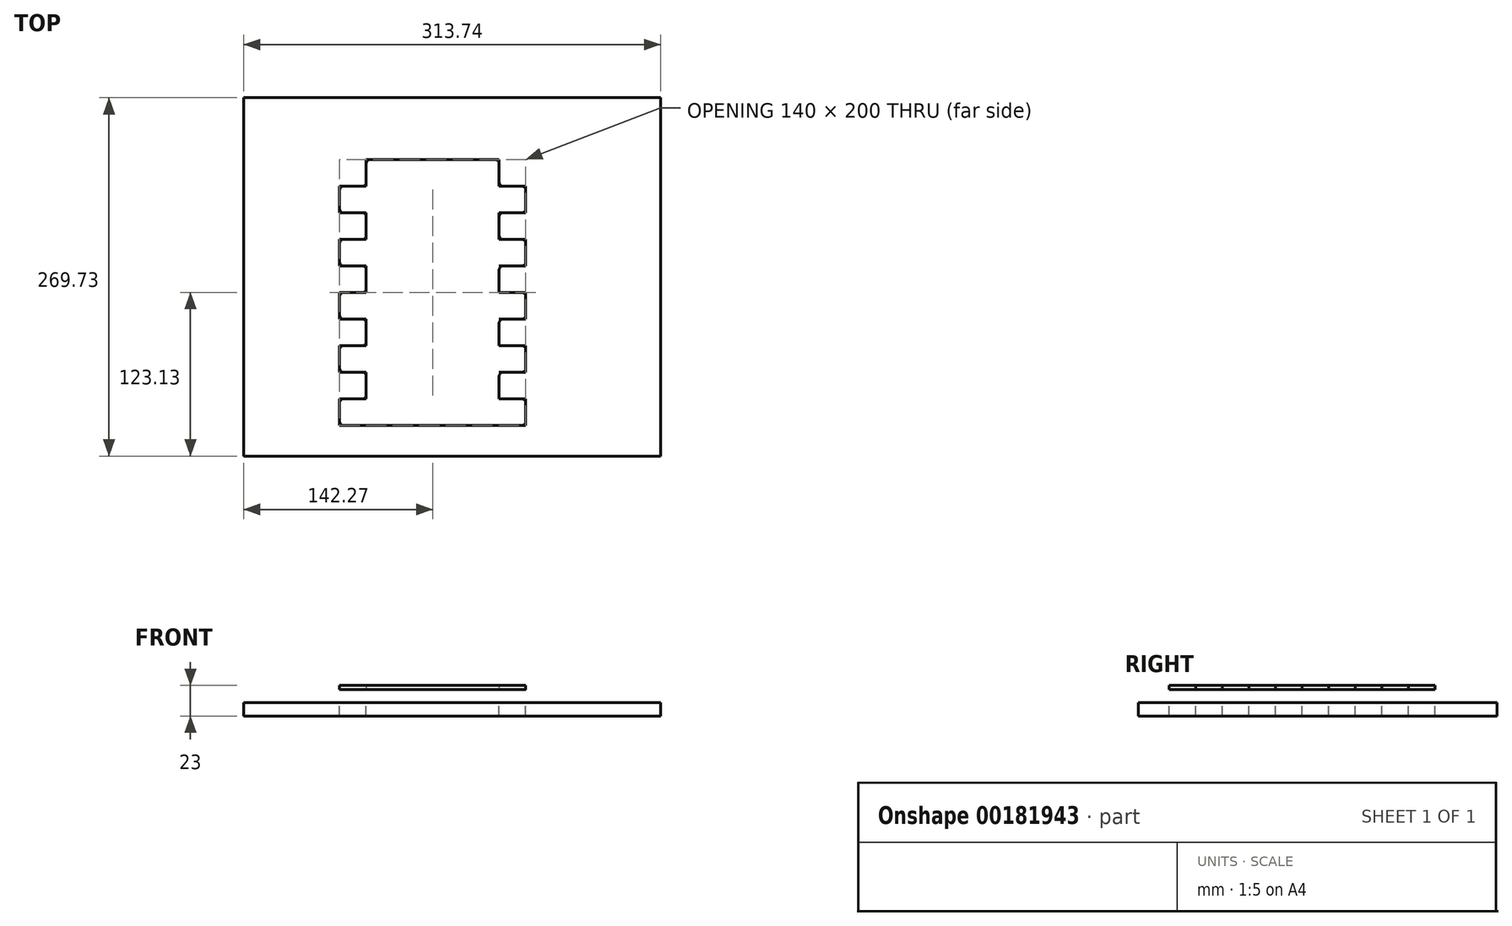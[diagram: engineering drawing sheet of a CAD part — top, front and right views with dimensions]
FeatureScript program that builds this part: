
annotation { "Feature Type Name" : "Feature", "Feature Type Description" : "" }
export const myFeature = defineFeature(function(context is Context, id is Id, definition is map)
    precondition{}
    {
        {
            var Q0;
            Q0=qCreatedBy(makeId("Top.planeOp"),FACE);
            var sketch = newSketch(context, id + "F0", { "sketchPlane" : qUnion([Q0])});
            skLineSegment(sketch, "E0.bottom", {"start": v(0, 0) * mm, "end": v(100, 0) * mm});
            skLineSegment(sketch, "E0.top", {"start": v(0, 200) * mm, "end": v(100, 200) * mm});
            skLineSegment(sketch, "E0.left", {"start": v(0, 0) * mm, "end": v(0, 200) * mm, "construction": true});
            skLineSegment(sketch, "E0.right", {"start": v(100, 0) * mm, "end": v(100, 200) * mm, "construction": true});
            skLineSegment(sketch, "E1.bottom", {"start": v(100, 0) * mm, "end": v(120, 0) * mm});
            skLineSegment(sketch, "E1.top", {"start": v(100, 20) * mm, "end": v(120, 20) * mm});
            skLineSegment(sketch, "E1.left", {"start": v(100, 0) * mm, "end": v(100, 20) * mm, "construction": true});
            skLineSegment(sketch, "E1.right", {"start": v(120, 0) * mm, "end": v(120, 20) * mm});
            skLineSegment(sketch, "E2", {"start": v(50, 0) * mm, "end": v(50, 200) * mm, "construction": true});
            skLineSegment(sketch, "E3.MirrorCS", {"start": v(0, 20) * mm, "end": v(-20, 20) * mm});
            skLineSegment(sketch, "E4.MirrorCS", {"start": v(-20, 0) * mm, "end": v(-20, 20) * mm});
            skLineSegment(sketch, "E5.MirrorCS", {"start": v(0, 0) * mm, "end": v(-20, 0) * mm});
            skLineSegment(sketch, "E6.0.1.0", {"start": v(100, 60) * mm, "end": v(120, 60) * mm});
            skLineSegment(sketch, "E6.0.1.1", {"start": v(120, 40) * mm, "end": v(120, 60) * mm});
            skLineSegment(sketch, "E6.0.1.2", {"start": v(100, 40) * mm, "end": v(120, 40) * mm});
            skLineSegment(sketch, "E6.0.1.3", {"start": v(0, 60) * mm, "end": v(-20, 60) * mm});
            skLineSegment(sketch, "E6.0.1.4", {"start": v(-20, 40) * mm, "end": v(-20, 60) * mm});
            skLineSegment(sketch, "E6.0.1.5", {"start": v(0, 40) * mm, "end": v(-20, 40) * mm});
            skLineSegment(sketch, "E6.0.2.0", {"start": v(100, 100) * mm, "end": v(120, 100) * mm});
            skLineSegment(sketch, "E6.0.2.1", {"start": v(120, 80) * mm, "end": v(120, 100) * mm});
            skLineSegment(sketch, "E6.0.2.2", {"start": v(100, 80) * mm, "end": v(120, 80) * mm});
            skLineSegment(sketch, "E6.0.2.3", {"start": v(0, 100) * mm, "end": v(-20, 100) * mm});
            skLineSegment(sketch, "E6.0.2.4", {"start": v(-20, 80) * mm, "end": v(-20, 100) * mm});
            skLineSegment(sketch, "E6.0.2.5", {"start": v(0, 80) * mm, "end": v(-20, 80) * mm});
            skLineSegment(sketch, "E6.0.3.0", {"start": v(100, 140) * mm, "end": v(120, 140) * mm});
            skLineSegment(sketch, "E6.0.3.1", {"start": v(120, 120) * mm, "end": v(120, 140) * mm});
            skLineSegment(sketch, "E6.0.3.2", {"start": v(100, 120) * mm, "end": v(120, 120) * mm});
            skLineSegment(sketch, "E6.0.3.3", {"start": v(0, 140) * mm, "end": v(-20, 140) * mm});
            skLineSegment(sketch, "E6.0.3.4", {"start": v(-20, 120) * mm, "end": v(-20, 140) * mm});
            skLineSegment(sketch, "E6.0.3.5", {"start": v(0, 120) * mm, "end": v(-20, 120) * mm});
            skLineSegment(sketch, "E6.0.4.0", {"start": v(100, 180) * mm, "end": v(120, 180) * mm});
            skLineSegment(sketch, "E6.0.4.1", {"start": v(120, 160) * mm, "end": v(120, 180) * mm});
            skLineSegment(sketch, "E6.0.4.2", {"start": v(100, 160) * mm, "end": v(120, 160) * mm});
            skLineSegment(sketch, "E6.0.4.3", {"start": v(0, 180) * mm, "end": v(-20, 180) * mm});
            skLineSegment(sketch, "E6.0.4.4", {"start": v(-20, 160) * mm, "end": v(-20, 180) * mm});
            skLineSegment(sketch, "E6.0.4.5", {"start": v(0, 160) * mm, "end": v(-20, 160) * mm});
            skLineSegment(sketch, "E6.direction1", {"start": v(100, 20) * mm, "end": v(125, 20) * mm, "construction": true});
            skLineSegment(sketch, "E6.direction2", {"start": v(100, 20) * mm, "end": v(100, 60) * mm, "construction": true});
            skLineSegment(sketch, "E7", {"start": v(0, 200) * mm, "end": v(0, 180) * mm});
            skLineSegment(sketch, "E8", {"start": v(100, 180) * mm, "end": v(100, 200) * mm});
            skLineSegment(sketch, "E9", {"start": v(100, 20) * mm, "end": v(100, 40) * mm});
            skLineSegment(sketch, "E10", {"start": v(100, 60) * mm, "end": v(100, 80) * mm});
            skLineSegment(sketch, "E11", {"start": v(100, 100) * mm, "end": v(100, 120) * mm});
            skLineSegment(sketch, "E12", {"start": v(100, 140) * mm, "end": v(100, 160) * mm});
            skLineSegment(sketch, "E13", {"start": v(0, 140) * mm, "end": v(0, 160) * mm});
            skLineSegment(sketch, "E14", {"start": v(0, 120) * mm, "end": v(0, 100) * mm});
            skLineSegment(sketch, "E15", {"start": v(0, 80) * mm, "end": v(0, 100) * mm});
            skLineSegment(sketch, "E16", {"start": v(0, 40) * mm, "end": v(0, 20) * mm});
            skLineSegment(sketch, "E17", {"start": v(0, 60) * mm, "end": v(0, 80) * mm});
            skLineSegment(sketch, "E18.bottom", {"start": v(-92.27, -23.13) * mm, "end": v(221.47, -23.13) * mm});
            skLineSegment(sketch, "E18.top", {"start": v(-92.27, 246.6) * mm, "end": v(221.47, 246.6) * mm});
            skLineSegment(sketch, "E18.left", {"start": v(-92.27, -23.13) * mm, "end": v(-92.27, 246.6) * mm});
            skLineSegment(sketch, "E18.right", {"start": v(221.47, -23.13) * mm, "end": v(221.47, 246.6) * mm});
            skSolve(sketch);
        }
        {
            var Q0;
            Q0=makeQuery(id+"F0.imprint","IMPRINT",FACE,{"disambiguationData":[TD([[makeQuery(id+"F0.imprint","IMPRINT",EDGE,{"derivedFrom":sQuery(id+"F0.wireOp",EDGE,"E0.bottom")}),1.0]])]});
            var Q1;
            Q1=makeQuery(id+"F0.imprint","IMPRINT",FACE,{"disambiguationData":[TD([[makeQuery(id+"F0.imprint","IMPRINT",EDGE,{"derivedFrom":sQuery(id+"F0.wireOp",EDGE,"E6.0.2.3")}),1.0]])]});
            extrude(context, id + "F1", {"entities" : qUnion([Q0, Q1]), "depth" : 3 * mm});
        }
        {
            var Q0;
            Q0=makeQuery(id+"F1.opExtrude","SWEPT_EDGE",EDGE,{"disambiguationData":[OSD([sQuery(id+"F0.wireOp",EDGE,"E6.0.4.1"),sQuery(id+"F0.wireOp",EDGE,"E6.0.4.2")])]});
            var Q1;
            Q1=makeQuery(id+"F1.opExtrude","SWEPT_EDGE",EDGE,{"disambiguationData":[OSD([sQuery(id+"F0.wireOp",EDGE,"E6.0.4.2"),sQuery(id+"F0.wireOp",EDGE,"E12")])]});
            var Q2;
            Q2=makeQuery(id+"F1.opExtrude","SWEPT_EDGE",EDGE,{"disambiguationData":[OSD([sQuery(id+"F0.wireOp",EDGE,"E6.0.3.2"),sQuery(id+"F0.wireOp",EDGE,"E11")])]});
            var Q3;
            Q3=makeQuery(id+"F1.opExtrude","SWEPT_EDGE",EDGE,{"disambiguationData":[OSD([sQuery(id+"F0.wireOp",EDGE,"E6.0.2.2"),sQuery(id+"F0.wireOp",EDGE,"E10")])]});
            var Q4;
            Q4=makeQuery(id+"F1.opExtrude","SWEPT_EDGE",EDGE,{"disambiguationData":[OSD([sQuery(id+"F0.wireOp",EDGE,"E6.0.2.1"),sQuery(id+"F0.wireOp",EDGE,"E6.0.2.2")])]});
            var Q5;
            Q5=makeQuery(id+"F1.opExtrude","SWEPT_EDGE",EDGE,{"disambiguationData":[OSD([sQuery(id+"F0.wireOp",EDGE,"E6.0.1.1"),sQuery(id+"F0.wireOp",EDGE,"E6.0.1.2")])]});
            var Q6;
            Q6=makeQuery(id+"F1.opExtrude","SWEPT_EDGE",EDGE,{"disambiguationData":[OSD([sQuery(id+"F0.wireOp",EDGE,"E6.0.1.2"),sQuery(id+"F0.wireOp",EDGE,"E9")])]});
            var Q7;
            Q7=makeQuery(id+"F1.opExtrude","SWEPT_EDGE",EDGE,{"disambiguationData":[OSD([sQuery(id+"F0.wireOp",EDGE,"E1.bottom"),sQuery(id+"F0.wireOp",EDGE,"E1.right")])]});
            var Q8;
            Q8=makeQuery(id+"F1.opExtrude","SWEPT_EDGE",EDGE,{"disambiguationData":[OSD([sQuery(id+"F0.wireOp",EDGE,"E1.top"),sQuery(id+"F0.wireOp",EDGE,"E1.right")])]});
            var Q9;
            Q9=makeQuery(id+"F1.opExtrude","SWEPT_EDGE",EDGE,{"disambiguationData":[OSD([sQuery(id+"F0.wireOp",EDGE,"E6.0.1.0"),sQuery(id+"F0.wireOp",EDGE,"E6.0.1.1")])]});
            var Q10;
            Q10=makeQuery(id+"F1.opExtrude","SWEPT_EDGE",EDGE,{"disambiguationData":[OSD([sQuery(id+"F0.wireOp",EDGE,"E6.0.2.0"),sQuery(id+"F0.wireOp",EDGE,"E6.0.2.1")])]});
            var Q11;
            Q11=makeQuery(id+"F1.opExtrude","SWEPT_EDGE",EDGE,{"disambiguationData":[OSD([sQuery(id+"F0.wireOp",EDGE,"E6.0.3.1"),sQuery(id+"F0.wireOp",EDGE,"E6.0.3.2")])]});
            var Q12;
            Q12=makeQuery(id+"F1.opExtrude","SWEPT_EDGE",EDGE,{"disambiguationData":[OSD([sQuery(id+"F0.wireOp",EDGE,"E6.0.3.0"),sQuery(id+"F0.wireOp",EDGE,"E6.0.3.1")])]});
            var Q13;
            Q13=makeQuery(id+"F1.opExtrude","SWEPT_EDGE",EDGE,{"disambiguationData":[OSD([sQuery(id+"F0.wireOp",EDGE,"E6.0.4.0"),sQuery(id+"F0.wireOp",EDGE,"E6.0.4.1")])]});
            var Q14;
            Q14=makeQuery(id+"F1.opExtrude","SWEPT_EDGE",EDGE,{"disambiguationData":[OSD([sQuery(id+"F0.wireOp",EDGE,"E0.top"),sQuery(id+"F0.wireOp",EDGE,"E8")])]});
            var Q15;
            Q15=makeQuery(id+"F1.opExtrude","SWEPT_EDGE",EDGE,{"disambiguationData":[OSD([sQuery(id+"F0.wireOp",EDGE,"E6.0.1.4"),sQuery(id+"F0.wireOp",EDGE,"E6.0.1.5")])]});
            var Q16;
            Q16=makeQuery(id+"F1.opExtrude","SWEPT_EDGE",EDGE,{"disambiguationData":[OSD([sQuery(id+"F0.wireOp",EDGE,"E4.MirrorCS"),sQuery(id+"F0.wireOp",EDGE,"E5.MirrorCS")])]});
            var Q17;
            Q17=makeQuery(id+"F1.opExtrude","SWEPT_EDGE",EDGE,{"disambiguationData":[OSD([sQuery(id+"F0.wireOp",EDGE,"E6.0.2.4"),sQuery(id+"F0.wireOp",EDGE,"E6.0.2.5")])]});
            var Q18;
            Q18=makeQuery(id+"F1.opExtrude","SWEPT_EDGE",EDGE,{"disambiguationData":[OSD([sQuery(id+"F0.wireOp",EDGE,"E6.0.3.4"),sQuery(id+"F0.wireOp",EDGE,"E6.0.3.5")])]});
            var Q19;
            Q19=makeQuery(id+"F1.opExtrude","SWEPT_EDGE",EDGE,{"disambiguationData":[OSD([sQuery(id+"F0.wireOp",EDGE,"E6.0.4.4"),sQuery(id+"F0.wireOp",EDGE,"E6.0.4.5")])]});
            var Q20;
            Q20=makeQuery(id+"F1.opExtrude","SWEPT_EDGE",EDGE,{"disambiguationData":[OSD([sQuery(id+"F0.wireOp",EDGE,"E6.0.4.3"),sQuery(id+"F0.wireOp",EDGE,"E6.0.4.4")])]});
            var Q21;
            Q21=makeQuery(id+"F1.opExtrude","SWEPT_EDGE",EDGE,{"disambiguationData":[OSD([sQuery(id+"F0.wireOp",EDGE,"E6.0.4.3"),sQuery(id+"F0.wireOp",EDGE,"E7")])]});
            var Q22;
            Q22=makeQuery(id+"F1.opExtrude","SWEPT_EDGE",EDGE,{"disambiguationData":[OSD([sQuery(id+"F0.wireOp",EDGE,"E6.0.3.3"),sQuery(id+"F0.wireOp",EDGE,"E13")])]});
            var Q23;
            Q23=makeQuery(id+"F1.opExtrude","SWEPT_EDGE",EDGE,{"disambiguationData":[OSD([sQuery(id+"F0.wireOp",EDGE,"E6.0.2.3"),sQuery(id+"F0.wireOp",EDGE,"E14"),sQuery(id+"F0.wireOp",EDGE,"E15")])]});
            var Q24;
            Q24=makeQuery(id+"F1.opExtrude","SWEPT_EDGE",EDGE,{"disambiguationData":[OSD([sQuery(id+"F0.wireOp",EDGE,"E6.0.1.3"),sQuery(id+"F0.wireOp",EDGE,"E17")])]});
            var Q25;
            Q25=makeQuery(id+"F1.opExtrude","SWEPT_EDGE",EDGE,{"disambiguationData":[OSD([sQuery(id+"F0.wireOp",EDGE,"E3.MirrorCS"),sQuery(id+"F0.wireOp",EDGE,"E16")])]});
            var Q26;
            Q26=makeQuery(id+"F1.opExtrude","SWEPT_EDGE",EDGE,{"disambiguationData":[OSD([sQuery(id+"F0.wireOp",EDGE,"E6.0.3.5"),sQuery(id+"F0.wireOp",EDGE,"E14")])]});
            var Q27;
            Q27=makeQuery(id+"F1.opExtrude","SWEPT_EDGE",EDGE,{"disambiguationData":[OSD([sQuery(id+"F0.wireOp",EDGE,"E6.0.4.5"),sQuery(id+"F0.wireOp",EDGE,"E13")])]});
            var Q28;
            Q28=makeQuery(id+"F1.opExtrude","SWEPT_EDGE",EDGE,{"disambiguationData":[OSD([sQuery(id+"F0.wireOp",EDGE,"E6.0.1.5"),sQuery(id+"F0.wireOp",EDGE,"E16")])]});
            var Q29;
            Q29=makeQuery(id+"F1.opExtrude","SWEPT_EDGE",EDGE,{"disambiguationData":[OSD([sQuery(id+"F0.wireOp",EDGE,"E0.top"),sQuery(id+"F0.wireOp",EDGE,"E7")])]});
            var Q30;
            Q30=makeQuery(id+"F1.opExtrude","SWEPT_EDGE",EDGE,{"disambiguationData":[OSD([sQuery(id+"F0.wireOp",EDGE,"E3.MirrorCS"),sQuery(id+"F0.wireOp",EDGE,"E4.MirrorCS")])]});
            var Q31;
            Q31=makeQuery(id+"F1.opExtrude","SWEPT_EDGE",EDGE,{"disambiguationData":[OSD([sQuery(id+"F0.wireOp",EDGE,"E6.0.3.3"),sQuery(id+"F0.wireOp",EDGE,"E6.0.3.4")])]});
            var Q32;
            Q32=makeQuery(id+"F1.opExtrude","SWEPT_EDGE",EDGE,{"disambiguationData":[OSD([sQuery(id+"F0.wireOp",EDGE,"E6.0.2.3"),sQuery(id+"F0.wireOp",EDGE,"E6.0.2.4")])]});
            var Q33;
            Q33=makeQuery(id+"F1.opExtrude","SWEPT_EDGE",EDGE,{"disambiguationData":[OSD([sQuery(id+"F0.wireOp",EDGE,"E6.0.1.3"),sQuery(id+"F0.wireOp",EDGE,"E6.0.1.4")])]});
            var Q34;
            Q34=makeQuery(id+"F1.opExtrude","SWEPT_EDGE",EDGE,{"disambiguationData":[OSD([sQuery(id+"F0.wireOp",EDGE,"E6.0.3.0"),sQuery(id+"F0.wireOp",EDGE,"E12")])]});
            var Q35;
            Q35=makeQuery(id+"F1.opExtrude","SWEPT_EDGE",EDGE,{"disambiguationData":[OSD([sQuery(id+"F0.wireOp",EDGE,"E6.0.2.5"),sQuery(id+"F0.wireOp",EDGE,"E15"),sQuery(id+"F0.wireOp",EDGE,"E17")])]});
            var Q36;
            Q36=makeQuery(id+"F1.opExtrude","SWEPT_EDGE",EDGE,{"disambiguationData":[OSD([sQuery(id+"F0.wireOp",EDGE,"E6.0.4.0"),sQuery(id+"F0.wireOp",EDGE,"E8")])]});
            fillet(context, id + "F2", {"entities" : qUnion([Q0, Q1, Q2, Q3, Q4, Q5, Q6, Q7, Q8, Q9, Q10, Q11, Q12, Q13, Q14, Q15, Q16, Q17, Q18, Q19, Q20, Q21, Q22, Q23, Q24, Q25, Q26, Q27, Q28, Q29, Q30, Q31, Q32, Q33, Q34, Q35, Q36]), "radius" : 3 * mm, "tangentPropagation" : true, "allowEdgeOverflow" : false});
        }
        {
            var Q0;
            Q0=makeQuery(id+"F0.imprint","IMPRINT",FACE,{"disambiguationData":[TD([[makeQuery(id+"F0.imprint","IMPRINT",EDGE,{"derivedFrom":sQuery(id+"F0.wireOp",EDGE,"E0.bottom")}),-1.0]])]});
            extrude(context, id + "F3", {"entities" : qUnion([Q0]), "oppositeDirection" : true, "depth" : 20 * mm, "hasSecondDirection" : true, "secondDirectionOppositeDirection" : true, "secondDirectionDepth" : 10 * mm});
        }
    });
